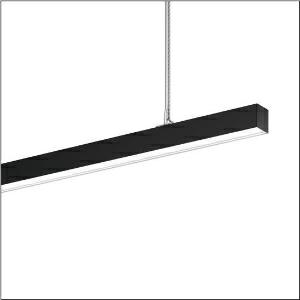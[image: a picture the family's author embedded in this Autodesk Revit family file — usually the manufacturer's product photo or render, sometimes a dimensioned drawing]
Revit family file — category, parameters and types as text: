
# Revit family: silica_21_51mx30db45bb
name_source: partatom
category: Lighting Fixtures
units: mm (PartAtom-declared; Revit-internal decimal feet)

## family parameters
Cut with Voids When Loaded = No
Host = Face
Light Source = No
Part Type = Normal
Room Calculation Point = No
Round Connector Dimension = Use Diameter
Shared = No

## types (1)
- --- (1 x LED, 5260 lm, 32 W, 4000K)
    Apparent Load = 32 VA
    CIE Flux Codes = 47 79 96 57 100
    Color Rendering = 80
    Color Temperature = 4000K
    Default Elevation = 1800 mm
    Description = Silica 21, office luminaire, primary optical cover: cover, of PMMA, opal, light emission: direct/indirect distribution, primary light characteristic: symmetric, installation type: suspended mounting, LED, rated luminous flux: 5.260lm, luminous efficacy: 164lm/W, light colour: 840, colour temperature: 4000K, control gear: DALI 2, with terminal, 3+2-pole, max. 2.5mm², mains connection: 220..240V, AC, 50/60Hz, rated input power: 32W, luminaire housing, of aluminium, matt jet black (RAL 9005), length: 1.504mm, width: 53mm, height: 53mm, protection rating (complete): IP20, insulation class (complete): insulation class I (protective earthing), certification: CE, permissible operating ambient temperature: 0..+35°C, standard: EN 50419, packaging unit: 1 piece
    Height = 53 mm
    Lamp = 1 x LED
    Lamp Light Flux = 5260 lm
    Lamp Power = 32 W
    Lamp count = 1
    Length = 1504 mm
    Luminous efficacy = 164 lm/W
    Manufacturer = Siteco
    ModVariant = No
    Model = 51MX30DB45BB
    Mounting Place = Ceiling
    Mounting Type = Pendant
    Number of Poles = 1
    OnlyDefault = Yes
    Power Factor = 1
    Product Name = Silica 21
    Product group = office luminaire | ceiling pendant
    ProductGroupID = 903
    Protection Class = Protection class I
    Protection Degree = IP 20
    RLX_Detail_Level = 1
    RLX_Emergency_Light_Flux = 0 lm
    RLX_Emergency_Type = 0
    RLX_Emergency_Type_DB = No
    RlxData = <blob elided: 26053 chars, md5=fe8da176>
    Socket = socket
    Standby Power = 0 W
    System Light Flux = 5260 lm
    System Power = 32 W
    Type Comments = factory setting: luminous flux: 100 % | dim-lin: 254 | 218 mA
    Type Image = l_1335856.jpg
    URL = http://relux.com
    VarID = @adj_118743
    Voltage = 0 V
    Weight = 0.00 kg
    Width = 53 mm

## geometry (parser evidence)
native form markers: Blend x4, Sweep x14
no freeform markers — native parametric forms only
